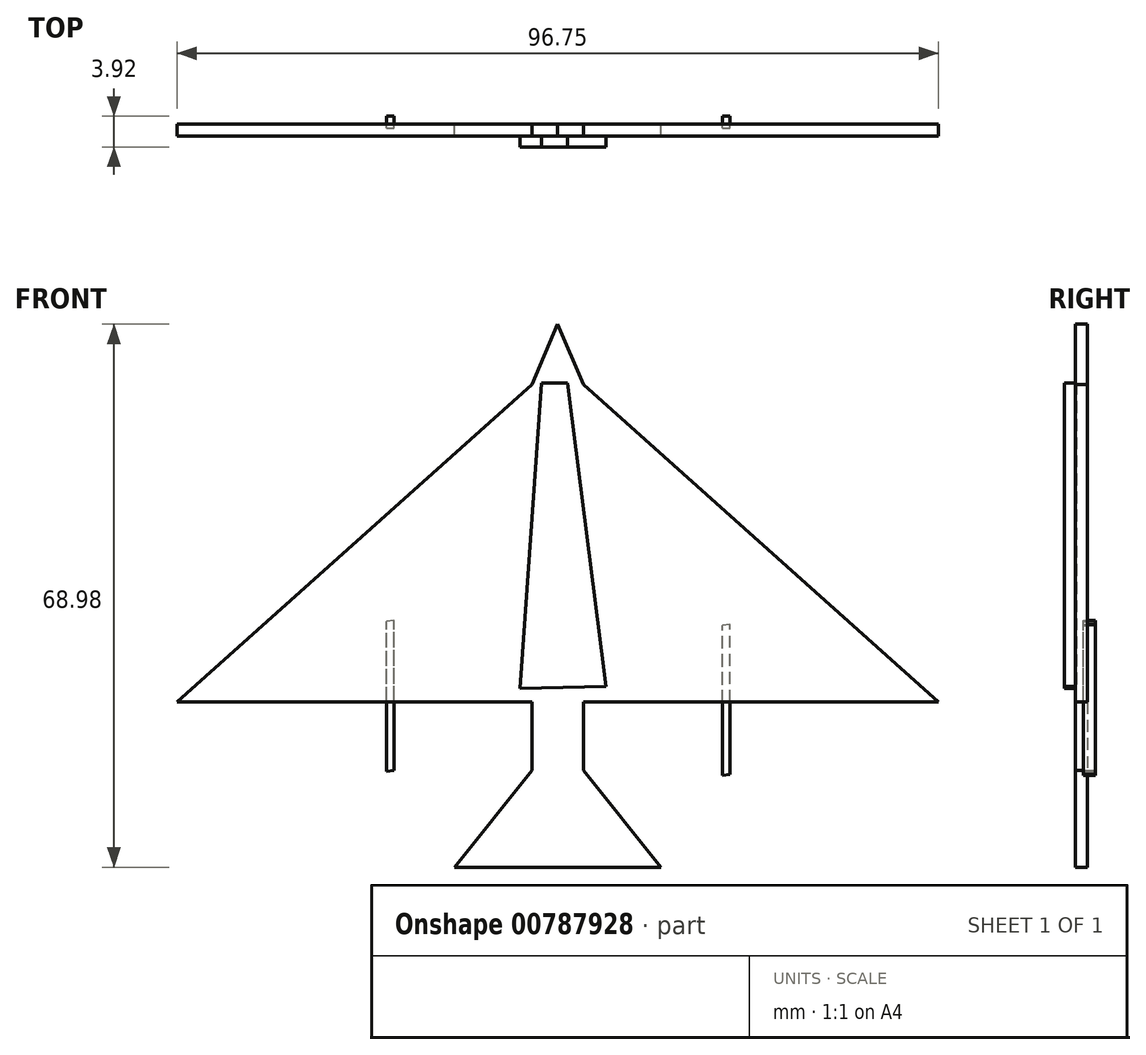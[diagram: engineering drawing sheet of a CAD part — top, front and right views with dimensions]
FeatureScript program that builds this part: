
annotation { "Feature Type Name" : "Feature", "Feature Type Description" : "" }
export const myFeature = defineFeature(function(context is Context, id is Id, definition is map)
    precondition{}
    {
        {
            var Q0;
            Q0=qCreatedBy(makeId("Front.planeOp"),FACE);
            var sketch = newSketch(context, id + "F0", { "sketchPlane" : qUnion([Q0])});
            skLineSegment(sketch, "E0.bottom", {"start": v(-25.09, 49.02) * mm, "end": v(-18.58, 49.02) * mm});
            skLineSegment(sketch, "E0.top", {"start": v(-25.09, -12.29) * mm, "end": v(-18.58, -12.29) * mm});
            skLineSegment(sketch, "E0.left", {"start": v(-25.09, 49.02) * mm, "end": v(-25.09, -12.29) * mm});
            skLineSegment(sketch, "E0.right", {"start": v(-18.58, 49.02) * mm, "end": v(-18.58, -12.29) * mm});
            skLineSegment(sketch, "E1", {"start": v(-25.09, 49.02) * mm, "end": v(-21.83, 56.69) * mm});
            skPoint(sketch, "E1.endSnap0", {"position": v(-21.83, 49.02) * mm});
            skLineSegment(sketch, "E2", {"start": v(-18.58, 49.02) * mm, "end": v(-21.83, 56.69) * mm});
            skLineSegment(sketch, "E3", {"start": v(-18.58, 49.02) * mm, "end": v(26.54, 8.71) * mm});
            skLineSegment(sketch, "E4", {"start": v(-25.09, 49.02) * mm, "end": v(-70.21, 8.71) * mm});
            skLineSegment(sketch, "E5", {"start": v(-70.21, 8.71) * mm, "end": v(-25.09, 8.71) * mm});
            skLineSegment(sketch, "E6", {"start": v(26.54, 8.71) * mm, "end": v(-18.58, 8.71) * mm});
            skLineSegment(sketch, "E7", {"start": v(-25.09, 0) * mm, "end": v(-34.94, -12.29) * mm});
            skLineSegment(sketch, "E8", {"start": v(-18.58, 0) * mm, "end": v(-8.73, -12.29) * mm});
            skLineSegment(sketch, "E9", {"start": v(-34.94, -12.29) * mm, "end": v(-8.73, -12.29) * mm});
            skLineSegment(sketch, "E10", {"start": v(-65.26, -46.45) * mm, "end": v(-62.48, -7.66) * mm});
            skLineSegment(sketch, "E11", {"start": v(-59.22, -7.66) * mm, "end": v(-54.29, -46.24) * mm});
            skLineSegment(sketch, "E12", {"start": v(-62.48, -7.66) * mm, "end": v(-59.22, -7.66) * mm});
            skLineSegment(sketch, "E13", {"start": v(-65.26, -46.45) * mm, "end": v(-54.29, -46.24) * mm});
            skLineSegment(sketch, "E14", {"start": v(26.01, -30.08) * mm, "end": v(26.01, -11.03) * mm});
            skLineSegment(sketch, "E15", {"start": v(26.01, -30.08) * mm, "end": v(26.94, -29.96) * mm});
            skLineSegment(sketch, "E16", {"start": v(26.94, -29.96) * mm, "end": v(26.94, -10.91) * mm});
            skLineSegment(sketch, "E17", {"start": v(26.94, -10.91) * mm, "end": v(26.01, -11.03) * mm});
            skSolve(sketch);
        }
        {
            var Q0;
            {var subQ5=sQuery(id+"F0.wireOp",EDGE,"E0.bottom");Q0=makeQuery(id+"F0.imprint","IMPRINT",FACE,{"disambiguationData":[TD([[makeQuery(id+"F0.imprint","IMPRINT",EDGE,{"derivedFrom":subQ5}),-1.0]])]});}
            var Q1;
            {var subQ0=sQuery(id+"F0.wireOp",EDGE,"E3");Q1=makeQuery(id+"F0.imprint","IMPRINT",FACE,{"disambiguationData":[TD([[makeQuery(id+"F0.imprint","IMPRINT",EDGE,{"derivedFrom":subQ0}),-1.0]])]});}
            var Q2;
            Q2=makeQuery(id+"F0.imprint","IMPRINT",FACE,{"disambiguationData":[TD([[makeQuery(id+"F0.imprint","IMPRINT",EDGE,{"derivedFrom":sQuery(id+"F0.wireOp",EDGE,"E0.bottom")}),1.0]])]});
            var Q3;
            {var subQ3=sQuery(id+"F0.wireOp",EDGE,"E7");Q3=makeQuery(id+"F0.imprint","IMPRINT",FACE,{"disambiguationData":[TD([[makeQuery(id+"F0.imprint","IMPRINT",EDGE,{"derivedFrom":subQ3}),1.0]])]});}
            var Q4;
            {var subQ3=sQuery(id+"F0.wireOp",EDGE,"E8");Q4=makeQuery(id+"F0.imprint","IMPRINT",FACE,{"disambiguationData":[TD([[makeQuery(id+"F0.imprint","IMPRINT",EDGE,{"derivedFrom":subQ3}),-1.0]])]});}
            var Q5;
            Q5=makeQuery(id+"F0.imprint","IMPRINT",FACE,{"disambiguationData":[TD([[makeQuery(id+"F0.imprint","IMPRINT",EDGE,{"derivedFrom":sQuery(id+"F0.wireOp",EDGE,"E10")}),-1.0]])]});
            var Q6;
            {var subQ0=sQuery(id+"F0.wireOp",EDGE,"E2");var subQ1=sQuery(id+"F0.wireOp",EDGE,"E1");var subQ2=makeQuery(id+"F0.imprint","INTERSECT",VERTEX,{"derivedFrom":[subQ1,subQ0]});Q6=makeQuery(id+"F0.imprint","IMPRINT",FACE,{"disambiguationData":[TD([[makeQuery(id+"F0.imprint","IMPRINT",EDGE,{"disambiguationData":[TD([[subQ2,1.0]])],"derivedFrom":subQ1}),-1.0]])]});}
            var Q7;
            {var subQ0=sQuery(id+"F0.wireOp",EDGE,"E4");Q7=makeQuery(id+"F0.imprint","IMPRINT",FACE,{"disambiguationData":[TD([[makeQuery(id+"F0.imprint","IMPRINT",EDGE,{"derivedFrom":subQ0}),1.0]])]});}
            var Q8;
            Q8=makeQuery(id+"F0.imprint","IMPRINT",FACE,{"disambiguationData":[TD([[makeQuery(id+"F0.imprint","IMPRINT",EDGE,{"derivedFrom":sQuery(id+"F0.wireOp",EDGE,"E14")}),-1.0]])]});
            var Q9;
            {var subQ6=sQuery(id+"F0.wireOp",EDGE,"E0.left");var subQ8=makeQuery(id+"F0.imprint","INTERSECT",VERTEX,{"derivedFrom":[subQ6,sQuery(id+"F0.wireOp",EDGE,"E7")]});Q9=makeQuery(id+"F0.imprint","IMPRINT",FACE,{"disambiguationData":[TD([[makeQuery(id+"F0.imprint","IMPRINT",EDGE,{"disambiguationData":[TD([[subQ8,1.0]])],"derivedFrom":subQ6}),1.0]])]});}
            var Q10;
            {var subQ4=sQuery(id+"F0.wireOp",EDGE,"E3");Q10=makeQuery(id+"F0.imprint","IMPRINT",FACE,{"disambiguationData":[TD([[makeQuery(id+"F0.imprint","IMPRINT",EDGE,{"derivedFrom":subQ4}),1.0]])]});}
            var Q11;
            {var subQ4=sQuery(id+"F0.wireOp",EDGE,"E4");Q11=makeQuery(id+"F0.imprint","IMPRINT",FACE,{"disambiguationData":[TD([[makeQuery(id+"F0.imprint","IMPRINT",EDGE,{"derivedFrom":subQ4}),-1.0]])]});}
            extrude(context, id + "F1", {"entities" : qUnion([Q0, Q1, Q2, Q3, Q4, Q5, Q6, Q7, Q8, Q9, Q10, Q11]), "depth" : 1.52 * mm, "offsetDistance" : 25.4 * mm});
        }
        {
            var Q0;
            Q0=makeQuery(id+"F1.opExtrude","SWEPT_BODY",BODY,{"disambiguationData":[OSD([sQuery(id+"F0.wireOp",EDGE,"E10"),sQuery(id+"F0.wireOp",EDGE,"E11"),sQuery(id+"F0.wireOp",EDGE,"E12"),sQuery(id+"F0.wireOp",EDGE,"E13")])]});
            transform(context, id + "F2", {"entities" : qUnion([Q0]), "transformType" : TransformType.TRANSLATION_3D, "dx" : 38.86 * mm, "dy" : -1.78 * mm, "dz" : 56.9 * mm, "makeCopy" : true});
        }
        {
            var Q0;
            Q0=makeQuery(id+"F1.opExtrude","SWEPT_BODY",BODY,{"disambiguationData":[OSD([sQuery(id+"F0.wireOp",EDGE,"E14"),sQuery(id+"F0.wireOp",EDGE,"E15"),sQuery(id+"F0.wireOp",EDGE,"E16"),sQuery(id+"F0.wireOp",EDGE,"E17")])]});
            transform(context, id + "F3", {"entities" : qUnion([Q0]), "transformType" : TransformType.TRANSLATION_3D, "dx" : -26.92 * mm, "dy" : 1.02 * mm, "dz" : 29.46 * mm, "makeCopy" : true});
        }
        {
            var Q0;
            Q0=makeQuery(id+"F3.opPattern","COPY",BODY,{"derivedFrom":makeQuery(id+"F1.opExtrude","SWEPT_BODY",BODY,{"disambiguationData":[OSD([sQuery(id+"F0.wireOp",EDGE,"E14"),sQuery(id+"F0.wireOp",EDGE,"E15"),sQuery(id+"F0.wireOp",EDGE,"E16"),sQuery(id+"F0.wireOp",EDGE,"E17")])]}),"instanceName":"1"});
            transform(context, id + "F4", {"entities" : qUnion([Q0]), "transformType" : TransformType.TRANSLATION_3D, "dx" : -42.67 * mm, "dy" : 0 * mm, "dz" : 0.5 * mm, "makeCopy" : true});
        }
        {
            var Q0;
            Q0=makeQuery(id+"F1.opExtrude","SWEPT_BODY",BODY,{"disambiguationData":[OSD([sQuery(id+"F0.wireOp",EDGE,"E14"),sQuery(id+"F0.wireOp",EDGE,"E15"),sQuery(id+"F0.wireOp",EDGE,"E16"),sQuery(id+"F0.wireOp",EDGE,"E17")])]});
            deleteBodies(context, id + "F5", {"entities" : qUnion([Q0])});
        }
        {
            var Q0;
            Q0=makeQuery(id+"F1.opExtrude","SWEPT_BODY",BODY,{"disambiguationData":[OSD([sQuery(id+"F0.wireOp",EDGE,"E10"),sQuery(id+"F0.wireOp",EDGE,"E11"),sQuery(id+"F0.wireOp",EDGE,"E12"),sQuery(id+"F0.wireOp",EDGE,"E13")])]});
            deleteBodies(context, id + "F6", {"entities" : qUnion([Q0])});
        }
        {
            var Q0;
            Q0=makeQuery(id+"F2.opPattern","COPY",BODY,{"derivedFrom":makeQuery(id+"F1.opExtrude","SWEPT_BODY",BODY,{"disambiguationData":[OSD([sQuery(id+"F0.wireOp",EDGE,"E10"),sQuery(id+"F0.wireOp",EDGE,"E11"),sQuery(id+"F0.wireOp",EDGE,"E12"),sQuery(id+"F0.wireOp",EDGE,"E13")])]}),"instanceName":"1"});
            transform(context, id + "F7", {"entities" : qUnion([Q0]), "transformType" : TransformType.TRANSLATION_3D, "dx" : -0.25 * mm, "dy" : 0.4 * mm, "dz" : 0 * mm, "makeCopy" : true});
        }
        {
            var Q0;
            Q0=makeQuery(id+"F2.opPattern","COPY",BODY,{"derivedFrom":makeQuery(id+"F1.opExtrude","SWEPT_BODY",BODY,{"disambiguationData":[OSD([sQuery(id+"F0.wireOp",EDGE,"E10"),sQuery(id+"F0.wireOp",EDGE,"E11"),sQuery(id+"F0.wireOp",EDGE,"E12"),sQuery(id+"F0.wireOp",EDGE,"E13")])]}),"instanceName":"1"});
            deleteBodies(context, id + "F8", {"entities" : qUnion([Q0])});
        }
    });
